# Revit family: Shower-Valve_Trim-KOHLER-Singulier-K-10879M
name_source: partatom
category: Plumbing Fixtures
revit_build: Autodesk Revit 2017 (Build: 20160225_1515(x64)
units: mm (PartAtom-declared; Revit-internal decimal feet)

## family parameters
Cut with Voids When Loaded = No
Host = Face
OmniClass Number = 23.31.25.00
OmniClass Title = Toilet and Bath Specialties
Part Type = Normal
Room Calculation Point = No
Round Connector Dimension = Use Diameter
Shared = No

## types (3) — shared parameters
ADA Compliant = No
Assembly Code = D2010700
CW Connection = Yes
Cold Water Inlet = Cold Water Inlet
Date Modified = 10/05/2020
Default Elevation = 42"
Description = 40 mm Bath/Shower Handle
Drain Included = No
Flow Rate = 0 GPM
HW Connection = Yes
Height = 6 11/16"
Hot Water Inlet = Hot Water Inlet
Length = 2 5/8"
Manufacturer = KOHLER Co.
Master Format 2014 = 22 42 23
Master Format 2014 Name = Residential Showers
Material = Brass construction
Pressure = 0.00 psi
Product Documentation Link = http://resources.kohler.com
Product Name = Singulier
Product Page URL = https://la.kohler.com
Tempered Water Outlet 1 = Tempered Water Outlet 1
Tempered Water Outlet 2 = Tempered Water Outlet 2
URL = https://la.kohler.com
Vent Connection = No
Waste Connection = No
Waste Water Outlet = Waste Water Outlet
WaterSense Certified = No
Width = 4 1/2"

## per-type parameters (varying)
| type | Finish | Model | Type |
| AF- Flange gold | Kohler-Metal-AF-Flange_Gold | K-10879M-4-AF | 1 |
| CP- Polished chrome | Kohler-Metal-CP-Polished_Chrome | K-10879M-4-CP | 2 |
| BN- Vibrant Brushed Nickel | Kohler-Metal-BN-Roman_Silver | K-10879M-4-BN | 3 |

## geometry (parser evidence)
native form markers: Sweep x6
no freeform markers — native parametric forms only
